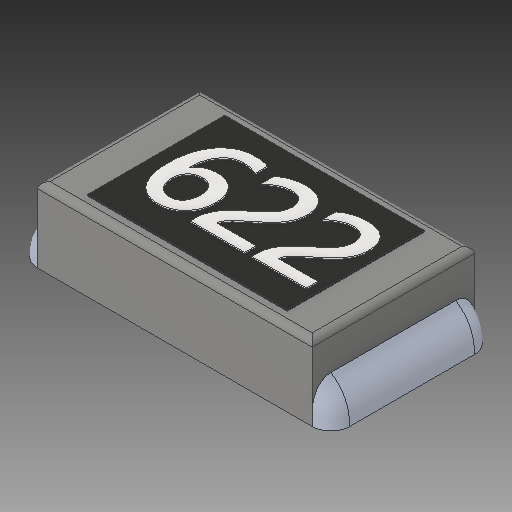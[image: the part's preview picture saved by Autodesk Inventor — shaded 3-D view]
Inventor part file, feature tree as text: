
AUTODESK INVENTOR PART (.ipt)
format: ipt  version: 2018.3 (Build 223284000, 284)  size: 282,624 bytes
history: native  units: mm
features: other x4, fillet x1, mirror x1
ambient origin geometry x8: Origin, YZ Plane, XZ Plane, XY Plane, X Axis, Y Axis, Z Axis, Center Point
bodies: Body1 (feature_tree), Body2 (feature_tree), Body3 (feature_tree)
feature tree (6):
  other  "Sólido1"
  other  "Sólido2"
  other  "Sólido3"
  fillet  "Fillet2"  [1 undecoded]
  mirror  "Mirror1"
  other  "Boss-Extrude4"
note: 1 required parameter value undecoded (feature->parameter linkage not recoverable at this tier; creation-order binding heuristic only, values carry confidence <= 0.55)
